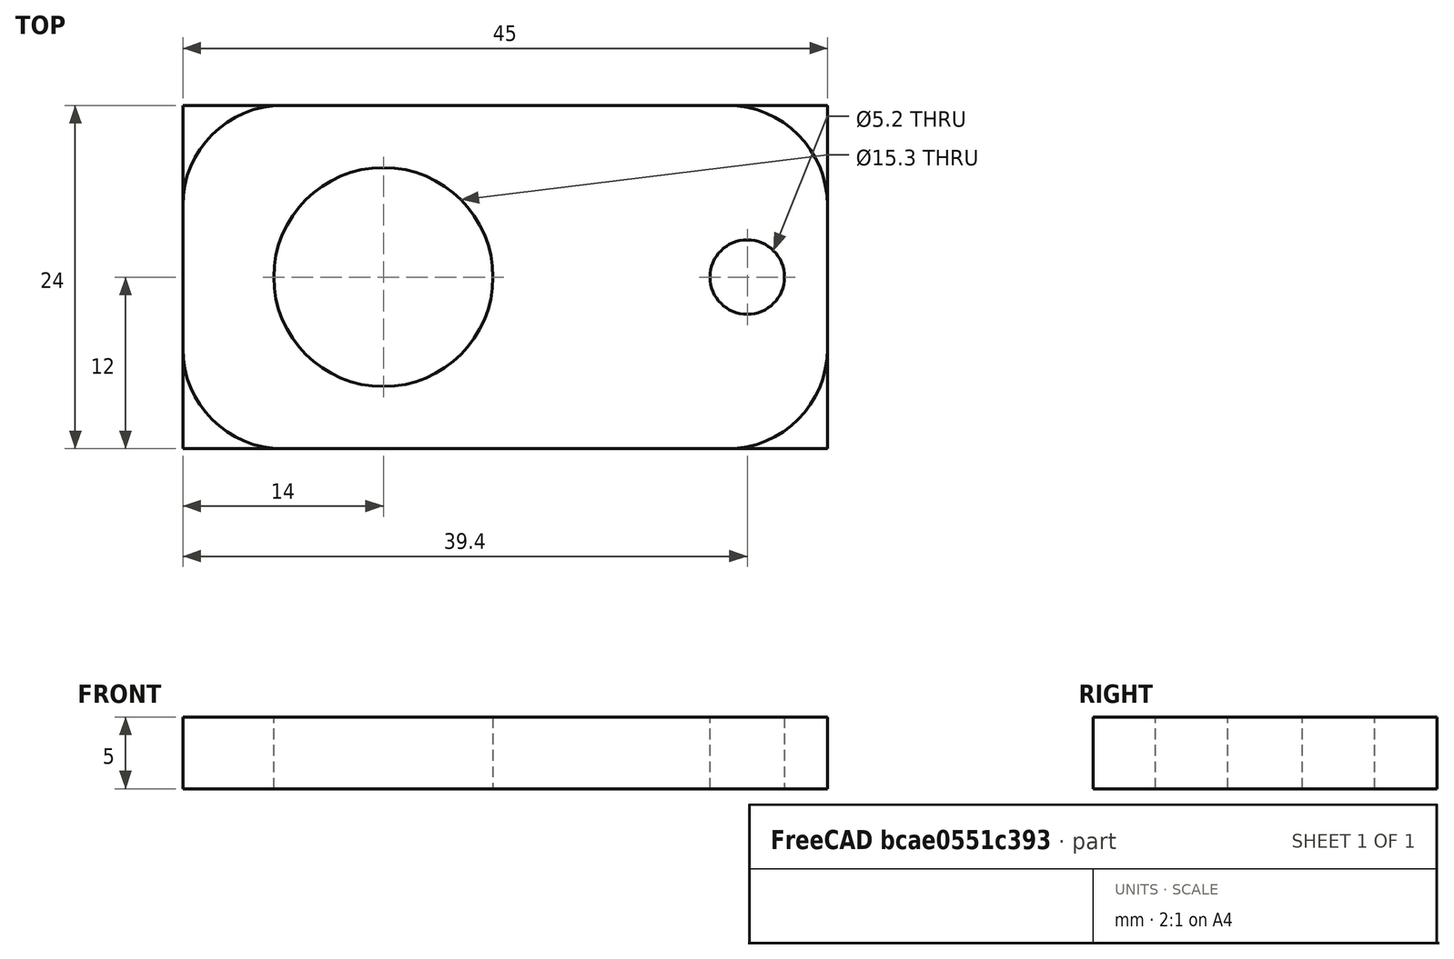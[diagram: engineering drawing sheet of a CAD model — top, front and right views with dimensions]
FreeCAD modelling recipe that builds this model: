
FCSTD DOCUMENT  (FreeCAD 0.16R)
Label: 25.4_oopspacer
License: All rights reserved
LicenseURL: http://en.wikipedia.org/wiki/All_rights_reserved
objects: Sketcher::SketchObject×2, PartDesign::Pad×1, PartDesign::Pocket×1, PartDesign::Fillet×1, Mesh::Feature×1
note: 7 computed .brp shape members not serialized (recipe doc carries the construction recipe); baked Part::Feature solids carry a one-line shape summary decoded from their .brp

FEATURE [Sketcher::SketchObject] Sketch
  sketch-geometry (4):
    g0: LineSegment StartX=-14 StartY=12 StartZ=0 EndX=31 EndY=12 EndZ=0
    g1: LineSegment StartX=31 StartY=12 StartZ=0 EndX=31 EndY=-12 EndZ=0
    g2: LineSegment StartX=31 StartY=-12 StartZ=0 EndX=-14 EndY=-12 EndZ=0
    g3: LineSegment StartX=-14 StartY=-12 StartZ=0 EndX=-14 EndY=12 EndZ=0
  constraints (12):
    c: Coincident(g0,g1)
    c: Coincident(g1,g2)
    c: Coincident(g2,g3)
    c: Coincident(g3,g0)
    c: Horizontal(g0)
    c: Horizontal(g2)
    c: Vertical(g1)
    c: Vertical(g3)
    c: Distance(g1) = 24
    c: Distance(g0) = 45
    c: Symmetric(g2,g0,g-1)
    c: DistanceX(g2) = -14
FEATURE [PartDesign::Pad] Pad
  Length = 5
  Length2 = 100
  Sketch = -> Sketch
  Type = 0
FEATURE [Sketcher::SketchObject] Sketch001
  Placement = pos=(0,0,5) rot=(0,0,1;0rad)
  Support = -> Pad [Face6]
  sketch-geometry (2):
    g0: Circle CenterX=0 CenterY=0 CenterZ=0 NormalX=0 NormalY=0 NormalZ=1 Radius=7.65
    g1: Circle CenterX=25.4 CenterY=0 CenterZ=0 NormalX=0 NormalY=0 NormalZ=1 Radius=2.6
  constraints (6):
    c: PointOnObject(g0,g-1)
    c: Radius(g0) = 7.65
    c: Coincident(g0,g-1)
    c: Radius(g1) = 2.6
    c: PointOnObject(g1,g-1)
    c: DistanceX(g1) = 25.4
FEATURE [PartDesign::Pocket] Pocket
  Length = 5
  Sketch = -> Sketch001
  Type = 1
FEATURE [PartDesign::Fillet] Fillet
  Base = -> Pocket [Edge1,Edge5,Edge2,Edge8]
  Radius = 7
FEATURE [Mesh::Feature] Mesh  label="Fillet (Meshed)"
